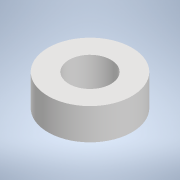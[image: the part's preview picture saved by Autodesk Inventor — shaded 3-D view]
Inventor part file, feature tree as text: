
AUTODESK INVENTOR PART (.ipt)
format: ipt  version: 2022 (Build 260153000, 153)  size: 96,256 bytes
history: native  units: in
note: dims shown in document units (in); Inventor stores cm internally (conversion verified against a paired STEP export)
features: extrude x1, sketch x1
ambient origin geometry x8: Origin, YZ Plane, XZ Plane, XY Plane, X Axis, Y Axis, Z Axis, Center Point
bodies: Solid1 (feature_tree)
feature tree (2):
  extrude  "Extrusion1"  Depth=0.1866in
  sketch  "Sketch1"  dims[d0=0.4988in d1=0.2492in d2=0.1866in d3=0.0in]
